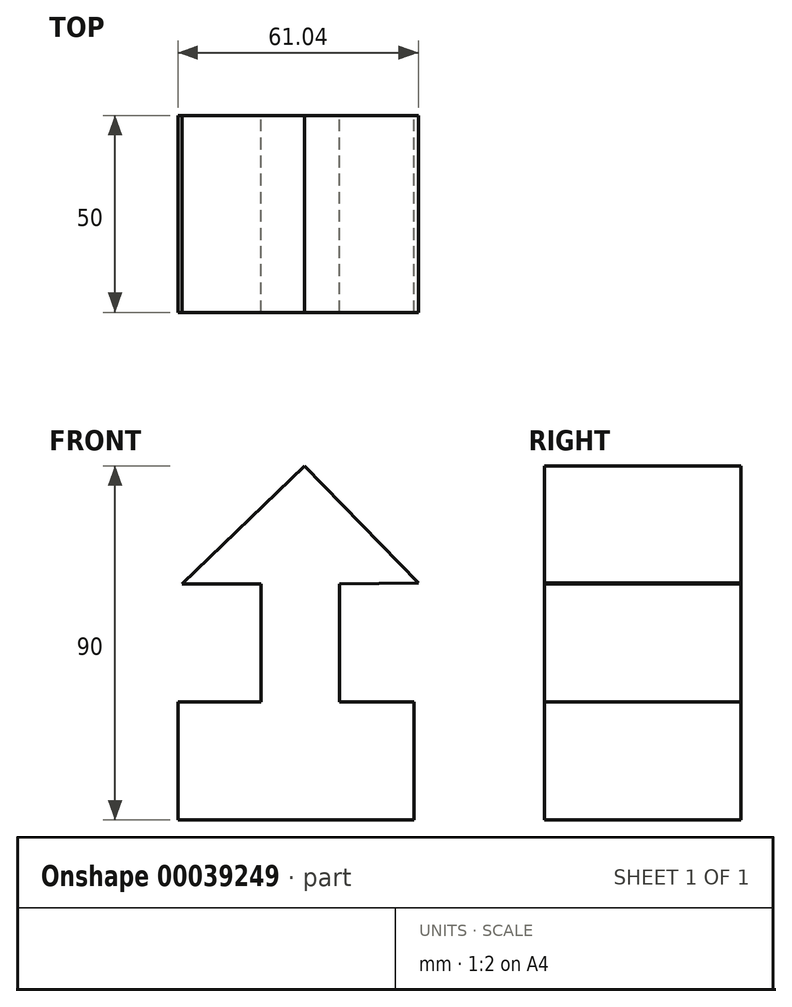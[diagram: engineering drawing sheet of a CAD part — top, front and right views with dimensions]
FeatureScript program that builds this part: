
annotation { "Feature Type Name" : "Feature", "Feature Type Description" : "" }
export const myFeature = defineFeature(function(context is Context, id is Id, definition is map)
    precondition{}
    {
        {
            var Q0;
            Q0=qCreatedBy(makeId("Front.planeOp"),FACE);
            var sketch = newSketch(context, id + "F0", { "sketchPlane" : qUnion([Q0])});
            skLineSegment(sketch, "E0.bottom", {"start": v(-26.82, 26.35) * mm, "end": v(-5.78, 26.35) * mm});
            skLineSegment(sketch, "E0.top", {"start": v(-26.82, -3.65) * mm, "end": v(33.18, -3.65) * mm});
            skLineSegment(sketch, "E0.left", {"start": v(-26.82, 26.35) * mm, "end": v(-26.82, -3.65) * mm});
            skLineSegment(sketch, "E0.right", {"start": v(33.18, 26.35) * mm, "end": v(33.18, -3.65) * mm});
            skLineSegment(sketch, "E1.left", {"start": v(-5.78, 26.35) * mm, "end": v(-5.78, 56.35) * mm});
            skLineSegment(sketch, "E1.right", {"start": v(14.22, 26.35) * mm, "end": v(14.22, 56.35) * mm});
            skLineSegment(sketch, "E2", {"start": v(-5.78, 56.35) * mm, "end": v(-25.78, 56.35) * mm});
            skLineSegment(sketch, "E3", {"start": v(-25.78, 56.35) * mm, "end": v(5.36, 86.35) * mm});
            skLineSegment(sketch, "E4", {"start": v(5.36, 86.35) * mm, "end": v(34.22, 56.6) * mm});
            skLineSegment(sketch, "E5", {"start": v(34.22, 56.6) * mm, "end": v(14.22, 56.35) * mm});
            skLineSegment(sketch, "E6.trimOffspring", {"start": v(14.22, 26.35) * mm, "end": v(33.18, 26.35) * mm});
            skSolve(sketch);
        }
        {
            var Q0;
            Q0=makeQuery(id+"F0.imprint","IMPRINT",FACE,{"disambiguationData":[TD([[makeQuery(id+"F0.imprint","IMPRINT",EDGE,{"derivedFrom":sQuery(id+"F0.wireOp",EDGE,"E0.bottom")}),-1.0]])]});
            extrude(context, id + "F1", {"entities" : qUnion([Q0]), "depth" : 50 * mm});
        }
    });
